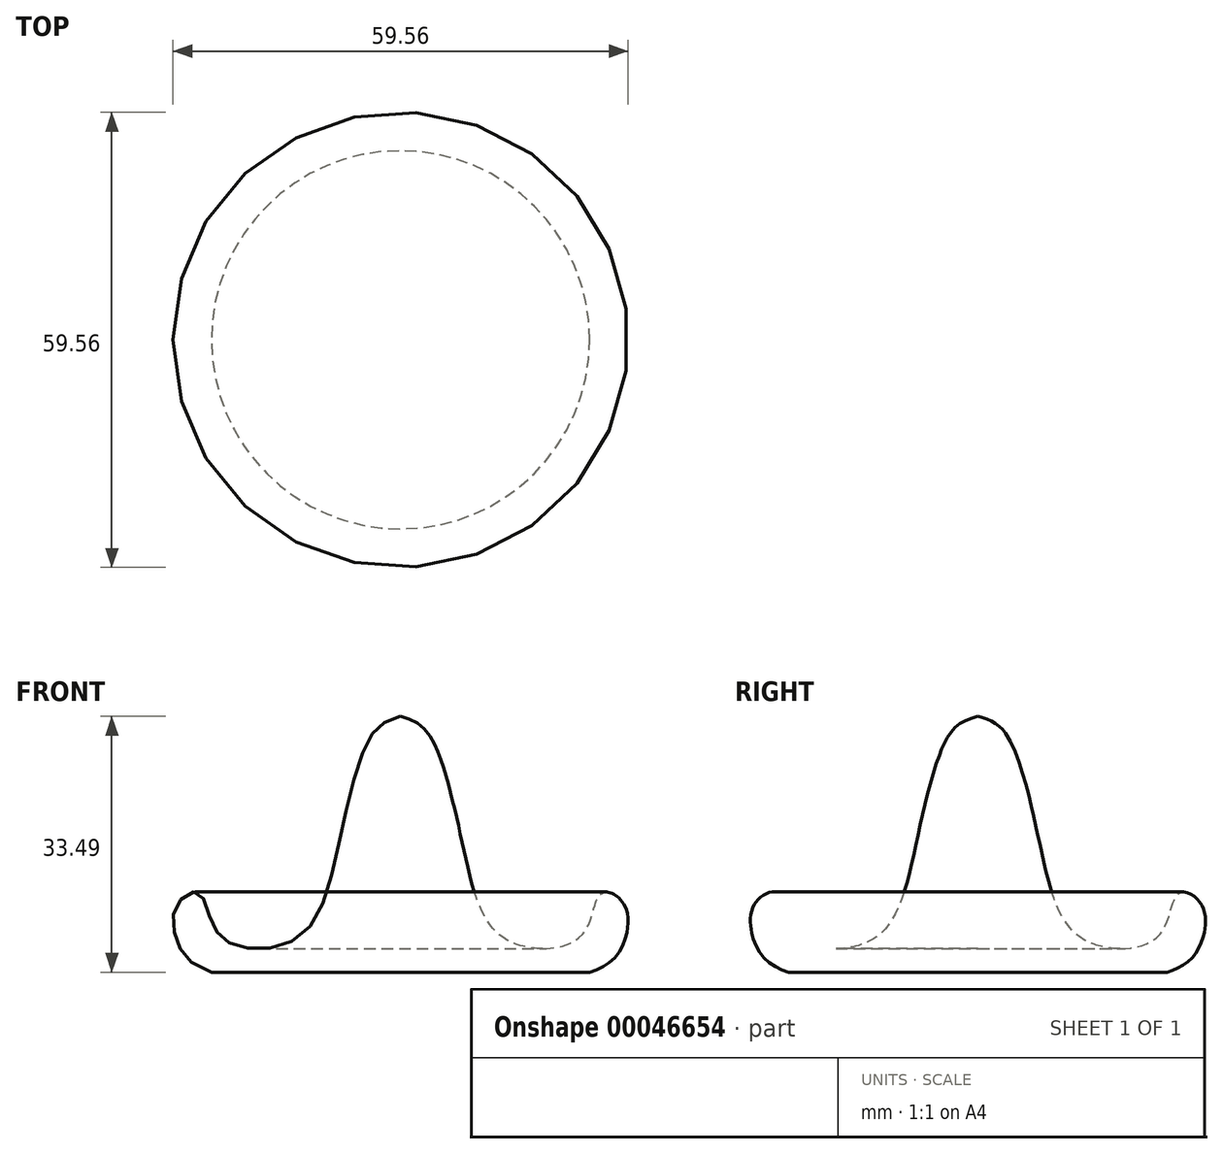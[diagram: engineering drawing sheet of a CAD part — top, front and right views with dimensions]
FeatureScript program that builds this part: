
annotation { "Feature Type Name" : "Feature", "Feature Type Description" : "" }
export const myFeature = defineFeature(function(context is Context, id is Id, definition is map)
    precondition{}
    {
        {
            var Q0;
            Q0=qCreatedBy(makeId("Front.planeOp"),FACE);
            var sketch = newSketch(context, id + "F0", { "sketchPlane" : qUnion([Q0])});
            skLineSegment(sketch, "E0", {"start": v(0, 0) * mm, "end": v(-24.75, 0) * mm});
            skFitSpline(sketch, "E1", {"points": [v(-24.75, 0) * mm, v(-29.25, 3.98) * mm, v(-29.25, 8.85) * mm, v(-26.43, 10.4) * mm, v(-24.6, 6.2) * mm, v(-20.9, 3.34) * mm, v(-12.96, 4.88) * mm, v(-7.96, 17.41) * mm, v(-3.85, 30.92) * mm, v(0, 33.49) * mm], "startDerivative": vector(-78.44, 23.93) * mm, "endDerivative": vector(58.87, 15.9) * mm});
            skSolve(sketch);
        }
        {
            var Q0;
            Q0=qCreatedBy(makeId("Front.planeOp"),FACE);
            var sketch = newSketch(context, id + "F1", { "sketchPlane" : qUnion([Q0])});
            skLineSegment(sketch, "E2", {"start": v(0, 67.43) * mm, "end": v(0, -35.37) * mm});
            skSolve(sketch);
        }
        {
            var Q0;
            Q0 = qSketchRegion(id + "F0", true);
            var Q1;
            Q1=sQuery(id+"F0.wireOp",EDGE,"E1");
            var Q2;
            Q2=sQuery(id+"F0.wireOp",EDGE,"E0");
            var Q3;
            Q3=sQuery(id+"F1.wireOp",EDGE,"E2");
            revolve(context, id + "F2", {"bodyType" : ToolBodyType.SURFACE, "entities" : qUnion([Q0]), "surfaceEntities" : qUnion([Q1, Q2]), "axis" : qUnion([Q3]), "revolveType" : RevolveType.FULL});
        }
    });
